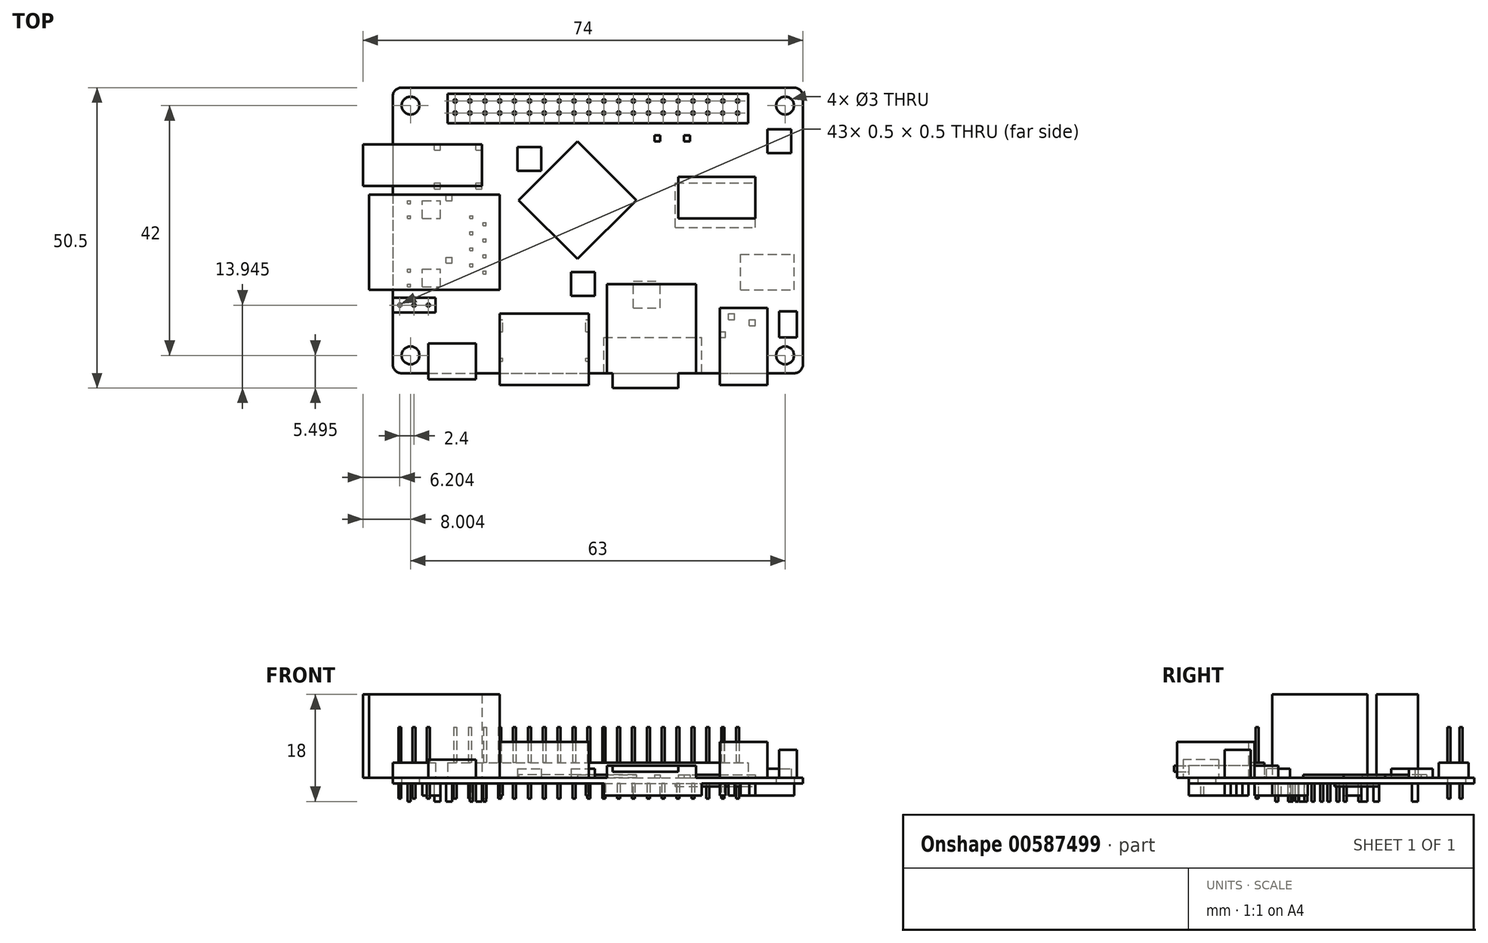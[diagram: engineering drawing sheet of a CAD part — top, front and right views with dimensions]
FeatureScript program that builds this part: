
annotation { "Feature Type Name" : "Feature", "Feature Type Description" : "" }
export const myFeature = defineFeature(function(context is Context, id is Id, definition is map)
    precondition{}
    {
        {
            var Q0;
            Q0=qCreatedBy(makeId("Top.planeOp"),FACE);
            var sketch = newSketch(context, id + "F0", { "sketchPlane" : qUnion([Q0])});
            skLineSegment(sketch, "E0.bottom", {"start": v(-42.34, 28.44) * mm, "end": v(23.66, 28.44) * mm});
            skLineSegment(sketch, "E0.top", {"start": v(-42.34, -19.56) * mm, "end": v(23.66, -19.56) * mm});
            skLineSegment(sketch, "E0.left", {"start": v(-43.84, 26.94) * mm, "end": v(-43.84, -18.06) * mm});
            skLineSegment(sketch, "E0.right", {"start": v(25.16, 26.94) * mm, "end": v(25.16, -18.06) * mm});
            skPoint(sketch, "E1", {"position": v(-43.84, 28.44) * mm});
            skCircle(sketch, "E2", {"center": v(-40.84, 25.44) * mm, "radius": 1.5 * mm});
            skCircle(sketch, "E3", {"center": v(22.16, 25.44) * mm, "radius": 1.5 * mm});
            skCircle(sketch, "E4", {"center": v(22.16, -16.56) * mm, "radius": 1.5 * mm});
            skCircle(sketch, "E5", {"center": v(-40.84, -16.56) * mm, "radius": 1.5 * mm});
            skLineSegment(sketch, "E6.bottom", {"start": v(-37.84, -19.56) * mm, "end": v(19.16, -19.56) * mm});
            skPoint(sketch, "E7.visualSharp", {"position": v(25.16, 28.44) * mm});
            skArc(sketch, "E7.filletArc", {"start": v(25.16, 26.94) * mm, "mid": v(24.72, 28) * mm, "end": v(23.66, 28.44) * mm});
            skArc(sketch, "E8.filletArc", {"start": v(-42.34, 28.44) * mm, "mid": v(-43.4, 28) * mm, "end": v(-43.84, 26.94) * mm});
            skPoint(sketch, "E9.visualSharp", {"position": v(-43.84, -19.56) * mm});
            skArc(sketch, "E9.filletArc", {"start": v(-43.84, -18.06) * mm, "mid": v(-43.4, -19.13) * mm, "end": v(-42.34, -19.56) * mm});
            skPoint(sketch, "E10.visualSharp", {"position": v(25.16, -19.56) * mm});
            skArc(sketch, "E10.filletArc", {"start": v(23.66, -19.56) * mm, "mid": v(24.72, -19.13) * mm, "end": v(25.16, -18.06) * mm});
            skSolve(sketch);
        }
        {
            var Q0;
            Q0=makeQuery(id+"F0.imprint","IMPRINT",FACE,{"disambiguationData":[TD([[makeQuery(id+"F0.imprint","IMPRINT",EDGE,{"derivedFrom":sQuery(id+"F0.wireOp",EDGE,"E0.bottom")}),-1.0]])]});
            extrude(context, id + "F1", {"entities" : qUnion([Q0]), "depth" : 1 * mm});
        }
        {
            var Q0;
            Q0=makeQuery(id+"F1.opExtrude","CAP_FACE",FACE,{"disambiguationData":[OSD([sQuery(id+"F0.wireOp",EDGE,"E0.bottom"),sQuery(id+"F0.wireOp",EDGE,"E0.top"),sQuery(id+"F0.wireOp",EDGE,"E0.left"),sQuery(id+"F0.wireOp",EDGE,"E0.right"),sQuery(id+"F0.wireOp",EDGE,"E2"),sQuery(id+"F0.wireOp",EDGE,"E3"),sQuery(id+"F0.wireOp",EDGE,"E4"),sQuery(id+"F0.wireOp",EDGE,"E5"),sQuery(id+"F0.wireOp",EDGE,"E6.bottom"),sQuery(id+"F0.wireOp",EDGE,"E7.filletArc"),sQuery(id+"F0.wireOp",EDGE,"E8.filletArc"),sQuery(id+"F0.wireOp",EDGE,"E9.filletArc"),sQuery(id+"F0.wireOp",EDGE,"E10.filletArc")])],"isStart":false});
            var sketch = newSketch(context, id + "F2", { "sketchPlane" : qUnion([Q0])});
            skLineSegment(sketch, "E11.bottom", {"start": v(24.16, -13.56) * mm, "end": v(21.16, -13.56) * mm});
            skLineSegment(sketch, "E11.top", {"start": v(24.16, -9.16) * mm, "end": v(21.16, -9.16) * mm});
            skLineSegment(sketch, "E11.left", {"start": v(24.16, -13.56) * mm, "end": v(24.16, -9.16) * mm});
            skLineSegment(sketch, "E11.right", {"start": v(21.16, -13.56) * mm, "end": v(21.16, -9.16) * mm});
            skSolve(sketch);
        }
        {
            var Q0;
            Q0=makeQuery(id+"F2.imprint","IMPRINT",FACE,{"disambiguationData":[TD([[makeQuery(id+"F2.imprint","IMPRINT",EDGE,{"derivedFrom":sQuery(id+"F2.wireOp",EDGE,"E11.bottom")}),-1.0]])]});
            extrude(context, id + "F3", {"entities" : qUnion([Q0]), "operationType" : NewBodyOperationType.ADD, "depth" : 4.7 * mm});
        }
        {
            var Q0;
            Q0=makeQuery(id+"F3.opExtrude","SWEPT_FACE",FACE,{"disambiguationData":[OSD([sQuery(id+"F2.wireOp",EDGE,"E11.left")])]});
            var sketch = newSketch(context, id + "F4", { "sketchPlane" : qUnion([Q0])});
            skCircle(sketch, "E12", {"center": v(-11.39, 3.44) * mm, "radius": 1.05 * mm});
            skSolve(sketch);
        }
        {
            var Q0;
            Q0=sQuery(id+"F4.wireOp",EDGE,"E12");
            extrude(context, id + "F5", {"bodyType" : ToolBodyType.SURFACE, "surfaceEntities" : qUnion([Q0]), "depth" : 2 * mm});
        }
        {
            var Q0;
            Q0=makeQuery(id+"F1.opExtrude","CAP_FACE",FACE,{"disambiguationData":[OSD([sQuery(id+"F0.wireOp",EDGE,"E0.bottom"),sQuery(id+"F0.wireOp",EDGE,"E0.top"),sQuery(id+"F0.wireOp",EDGE,"E0.left"),sQuery(id+"F0.wireOp",EDGE,"E0.right"),sQuery(id+"F0.wireOp",EDGE,"E2"),sQuery(id+"F0.wireOp",EDGE,"E3"),sQuery(id+"F0.wireOp",EDGE,"E4"),sQuery(id+"F0.wireOp",EDGE,"E5"),sQuery(id+"F0.wireOp",EDGE,"E6.bottom"),sQuery(id+"F0.wireOp",EDGE,"E7.filletArc"),sQuery(id+"F0.wireOp",EDGE,"E8.filletArc"),sQuery(id+"F0.wireOp",EDGE,"E9.filletArc"),sQuery(id+"F0.wireOp",EDGE,"E10.filletArc")])],"isStart":false});
            var sketch = newSketch(context, id + "F6", { "sketchPlane" : qUnion([Q0])});
            skLineSegment(sketch, "E13.bottom", {"start": v(11.16, -8.56) * mm, "end": v(19.16, -8.56) * mm});
            skLineSegment(sketch, "E13.top", {"start": v(11.16, -21.56) * mm, "end": v(19.16, -21.56) * mm});
            skLineSegment(sketch, "E13.left", {"start": v(11.16, -8.56) * mm, "end": v(11.16, -21.56) * mm});
            skLineSegment(sketch, "E13.right", {"start": v(19.16, -8.56) * mm, "end": v(19.16, -21.56) * mm});
            skSolve(sketch);
        }
        {
            var Q0;
            Q0=qSketchRegion(id+"F6",true);
            extrude(context, id + "F7", {"entities" : qUnion([Q0]), "operationType" : NewBodyOperationType.ADD, "depth" : 6 * mm});
        }
        {
            var Q0;
            Q0=makeQuery(id+"F1.opExtrude","CAP_FACE",FACE,{"disambiguationData":[OSD([sQuery(id+"F0.wireOp",EDGE,"E0.bottom"),sQuery(id+"F0.wireOp",EDGE,"E0.top"),sQuery(id+"F0.wireOp",EDGE,"E0.left"),sQuery(id+"F0.wireOp",EDGE,"E0.right"),sQuery(id+"F0.wireOp",EDGE,"E2"),sQuery(id+"F0.wireOp",EDGE,"E3"),sQuery(id+"F0.wireOp",EDGE,"E4"),sQuery(id+"F0.wireOp",EDGE,"E5"),sQuery(id+"F0.wireOp",EDGE,"E6.bottom"),sQuery(id+"F0.wireOp",EDGE,"E7.filletArc"),sQuery(id+"F0.wireOp",EDGE,"E8.filletArc"),sQuery(id+"F0.wireOp",EDGE,"E9.filletArc"),sQuery(id+"F0.wireOp",EDGE,"E10.filletArc")])],"isStart":false});
            var sketch = newSketch(context, id + "F8", { "sketchPlane" : qUnion([Q0])});
            skLineSegment(sketch, "E14.bottom", {"start": v(-7.84, -4.56) * mm, "end": v(7.16, -4.56) * mm});
            skLineSegment(sketch, "E14.top", {"start": v(-7.84, -19.56) * mm, "end": v(7.16, -19.56) * mm});
            skLineSegment(sketch, "E14.left", {"start": v(-7.84, -4.56) * mm, "end": v(-7.84, -19.56) * mm});
            skLineSegment(sketch, "E14.right", {"start": v(7.16, -4.56) * mm, "end": v(7.16, -19.56) * mm});
            skSolve(sketch);
        }
        {
            var Q0;
            Q0=qSketchRegion(id+"F8",true);
            extrude(context, id + "F9", {"entities" : qUnion([Q0]), "operationType" : NewBodyOperationType.ADD, "depth" : 2 * mm});
        }
        {
            var Q0;
            Q0=makeQuery(id+"F9.boolean.opBoolean","MERGE",FACE,{"derivedFrom":[makeQuery(id+"F1.opExtrude","SWEPT_FACE",FACE,{"disambiguationData":[OSD([sQuery(id+"F0.wireOp",EDGE,"E0.top"),sQuery(id+"F0.wireOp",EDGE,"E6.bottom")])]}),makeQuery(id+"F9.opExtrude","SWEPT_FACE",FACE,{"disambiguationData":[OSD([sQuery(id+"F8.wireOp",EDGE,"E14.top")])]})]});
            var sketch = newSketch(context, id + "F10", { "sketchPlane" : qUnion([Q0])});
            skLineSegment(sketch, "E15.bottom", {"start": v(-6.84, 3) * mm, "end": v(4.16, 3) * mm});
            skLineSegment(sketch, "E15.top", {"start": v(-6.84, 2) * mm, "end": v(4.16, 2) * mm});
            skLineSegment(sketch, "E15.left", {"start": v(-6.84, 3) * mm, "end": v(-6.84, 2) * mm});
            skLineSegment(sketch, "E15.right", {"start": v(4.16, 3) * mm, "end": v(4.16, 2) * mm});
            skSolve(sketch);
        }
        {
            var Q0;
            Q0=qSketchRegion(id+"F10",true);
            extrude(context, id + "F11", {"entities" : qUnion([Q0]), "operationType" : NewBodyOperationType.ADD, "depth" : 2.5 * mm});
        }
        {
            var Q0;
            Q0=makeQuery(id+"F1.opExtrude","CAP_FACE",FACE,{"disambiguationData":[OSD([sQuery(id+"F0.wireOp",EDGE,"E0.bottom"),sQuery(id+"F0.wireOp",EDGE,"E0.top"),sQuery(id+"F0.wireOp",EDGE,"E0.left"),sQuery(id+"F0.wireOp",EDGE,"E0.right"),sQuery(id+"F0.wireOp",EDGE,"E2"),sQuery(id+"F0.wireOp",EDGE,"E3"),sQuery(id+"F0.wireOp",EDGE,"E4"),sQuery(id+"F0.wireOp",EDGE,"E5"),sQuery(id+"F0.wireOp",EDGE,"E6.bottom"),sQuery(id+"F0.wireOp",EDGE,"E7.filletArc"),sQuery(id+"F0.wireOp",EDGE,"E8.filletArc"),sQuery(id+"F0.wireOp",EDGE,"E9.filletArc"),sQuery(id+"F0.wireOp",EDGE,"E10.filletArc")])],"isStart":false});
            var sketch = newSketch(context, id + "F12", { "sketchPlane" : qUnion([Q0])});
            skLineSegment(sketch, "E16.bottom", {"start": v(-25.84, -9.56) * mm, "end": v(-10.84, -9.56) * mm});
            skLineSegment(sketch, "E16.top", {"start": v(-25.84, -21.56) * mm, "end": v(-10.84, -21.56) * mm});
            skLineSegment(sketch, "E16.left", {"start": v(-25.84, -9.56) * mm, "end": v(-25.84, -21.56) * mm});
            skLineSegment(sketch, "E16.right", {"start": v(-10.84, -9.56) * mm, "end": v(-10.84, -21.56) * mm});
            skSolve(sketch);
        }
        {
            var Q0;
            Q0=qSketchRegion(id+"F12",true);
            extrude(context, id + "F13", {"entities" : qUnion([Q0]), "operationType" : NewBodyOperationType.ADD, "depth" : 6 * mm});
        }
        {
            var Q0;
            Q0=makeQuery(id+"F1.opExtrude","CAP_FACE",FACE,{"disambiguationData":[OSD([sQuery(id+"F0.wireOp",EDGE,"E0.bottom"),sQuery(id+"F0.wireOp",EDGE,"E0.top"),sQuery(id+"F0.wireOp",EDGE,"E0.left"),sQuery(id+"F0.wireOp",EDGE,"E0.right"),sQuery(id+"F0.wireOp",EDGE,"E2"),sQuery(id+"F0.wireOp",EDGE,"E3"),sQuery(id+"F0.wireOp",EDGE,"E4"),sQuery(id+"F0.wireOp",EDGE,"E5"),sQuery(id+"F0.wireOp",EDGE,"E6.bottom"),sQuery(id+"F0.wireOp",EDGE,"E7.filletArc"),sQuery(id+"F0.wireOp",EDGE,"E8.filletArc"),sQuery(id+"F0.wireOp",EDGE,"E9.filletArc"),sQuery(id+"F0.wireOp",EDGE,"E10.filletArc")])],"isStart":false});
            var sketch = newSketch(context, id + "F14", { "sketchPlane" : qUnion([Q0])});
            skLineSegment(sketch, "E17.bottom", {"start": v(-37.84, -14.56) * mm, "end": v(-29.84, -14.56) * mm});
            skLineSegment(sketch, "E17.top", {"start": v(-37.84, -20.56) * mm, "end": v(-29.84, -20.56) * mm});
            skLineSegment(sketch, "E17.left", {"start": v(-37.84, -14.56) * mm, "end": v(-37.84, -20.56) * mm});
            skLineSegment(sketch, "E17.right", {"start": v(-29.84, -14.56) * mm, "end": v(-29.84, -20.56) * mm});
            skSolve(sketch);
        }
        {
            var Q0;
            Q0=qSketchRegion(id+"F14",true);
            extrude(context, id + "F15", {"entities" : qUnion([Q0]), "operationType" : NewBodyOperationType.ADD, "depth" : 3 * mm});
        }
        {
            var Q0;
            Q0=makeQuery(id+"F1.opExtrude","CAP_FACE",FACE,{"disambiguationData":[OSD([sQuery(id+"F0.wireOp",EDGE,"E0.bottom"),sQuery(id+"F0.wireOp",EDGE,"E0.top"),sQuery(id+"F0.wireOp",EDGE,"E0.left"),sQuery(id+"F0.wireOp",EDGE,"E0.right"),sQuery(id+"F0.wireOp",EDGE,"E2"),sQuery(id+"F0.wireOp",EDGE,"E3"),sQuery(id+"F0.wireOp",EDGE,"E4"),sQuery(id+"F0.wireOp",EDGE,"E5"),sQuery(id+"F0.wireOp",EDGE,"E6.bottom"),sQuery(id+"F0.wireOp",EDGE,"E7.filletArc"),sQuery(id+"F0.wireOp",EDGE,"E8.filletArc"),sQuery(id+"F0.wireOp",EDGE,"E9.filletArc"),sQuery(id+"F0.wireOp",EDGE,"E10.filletArc")])],"isStart":false});
            var sketch = newSketch(context, id + "F16", { "sketchPlane" : qUnion([Q0])});
            skLineSegment(sketch, "E18.bottom", {"start": v(-43.84, -6.86) * mm, "end": v(-36.64, -6.86) * mm});
            skLineSegment(sketch, "E18.top", {"start": v(-43.84, -9.36) * mm, "end": v(-36.64, -9.36) * mm});
            skLineSegment(sketch, "E18.left", {"start": v(-43.84, -6.86) * mm, "end": v(-43.84, -9.36) * mm});
            skLineSegment(sketch, "E18.right", {"start": v(-36.64, -6.86) * mm, "end": v(-36.64, -9.36) * mm});
            skSolve(sketch);
        }
        {
            var Q0;
            Q0=qSketchRegion(id+"F16",true);
            extrude(context, id + "F17", {"entities" : qUnion([Q0]), "operationType" : NewBodyOperationType.ADD, "depth" : 2.5 * mm});
        }
        {
            var Q0;
            Q0=makeQuery(id+"F17.opExtrude","CAP_FACE",FACE,{"disambiguationData":[OSD([sQuery(id+"F16.wireOp",EDGE,"E18.bottom"),sQuery(id+"F16.wireOp",EDGE,"E18.top"),sQuery(id+"F16.wireOp",EDGE,"E18.left"),sQuery(id+"F16.wireOp",EDGE,"E18.right")])],"isStart":false});
            var sketch = newSketch(context, id + "F18", { "sketchPlane" : qUnion([Q0])});
            skLineSegment(sketch, "E19.bottom", {"start": v(-42.89, -7.86) * mm, "end": v(-42.39, -7.86) * mm});
            skLineSegment(sketch, "E19.top", {"start": v(-42.89, -8.36) * mm, "end": v(-42.39, -8.36) * mm});
            skLineSegment(sketch, "E19.left", {"start": v(-42.89, -7.86) * mm, "end": v(-42.89, -8.36) * mm});
            skLineSegment(sketch, "E19.right", {"start": v(-42.39, -7.86) * mm, "end": v(-42.39, -8.36) * mm});
            skLineSegment(sketch, "E20.bottom", {"start": v(-40.49, -7.86) * mm, "end": v(-39.99, -7.86) * mm});
            skLineSegment(sketch, "E20.top", {"start": v(-40.49, -8.36) * mm, "end": v(-39.99, -8.36) * mm});
            skLineSegment(sketch, "E20.left", {"start": v(-40.49, -7.86) * mm, "end": v(-40.49, -8.36) * mm});
            skLineSegment(sketch, "E20.right", {"start": v(-39.99, -7.86) * mm, "end": v(-39.99, -8.36) * mm});
            skLineSegment(sketch, "E21.bottom", {"start": v(-38.09, -7.86) * mm, "end": v(-37.59, -7.86) * mm});
            skLineSegment(sketch, "E21.top", {"start": v(-38.09, -8.36) * mm, "end": v(-37.59, -8.36) * mm});
            skLineSegment(sketch, "E21.left", {"start": v(-38.09, -7.86) * mm, "end": v(-38.09, -8.36) * mm});
            skLineSegment(sketch, "E21.right", {"start": v(-37.59, -7.86) * mm, "end": v(-37.59, -8.36) * mm});
            skSolve(sketch);
        }
        {
            var Q0;
            Q0=qSketchRegion(id+"F18",true);
            extrude(context, id + "F19", {"entities" : qUnion([Q0]), "operationType" : NewBodyOperationType.ADD, "depth" : 6 * mm});
        }
        {
            var Q0;
            Q0=makeQuery(id+"F1.opExtrude","CAP_FACE",FACE,{"disambiguationData":[OSD([sQuery(id+"F0.wireOp",EDGE,"E0.bottom"),sQuery(id+"F0.wireOp",EDGE,"E0.top"),sQuery(id+"F0.wireOp",EDGE,"E0.left"),sQuery(id+"F0.wireOp",EDGE,"E0.right"),sQuery(id+"F0.wireOp",EDGE,"E2"),sQuery(id+"F0.wireOp",EDGE,"E3"),sQuery(id+"F0.wireOp",EDGE,"E4"),sQuery(id+"F0.wireOp",EDGE,"E5"),sQuery(id+"F0.wireOp",EDGE,"E6.bottom"),sQuery(id+"F0.wireOp",EDGE,"E7.filletArc"),sQuery(id+"F0.wireOp",EDGE,"E8.filletArc"),sQuery(id+"F0.wireOp",EDGE,"E9.filletArc"),sQuery(id+"F0.wireOp",EDGE,"E10.filletArc")])],"isStart":false});
            var sketch = newSketch(context, id + "F20", { "sketchPlane" : qUnion([Q0])});
            skLineSegment(sketch, "E22.bottom", {"start": v(-25.84, 10.44) * mm, "end": v(-47.84, 10.44) * mm});
            skLineSegment(sketch, "E22.top", {"start": v(-25.84, -5.56) * mm, "end": v(-47.84, -5.56) * mm});
            skLineSegment(sketch, "E22.left", {"start": v(-25.84, 10.44) * mm, "end": v(-25.84, -5.56) * mm});
            skLineSegment(sketch, "E22.right", {"start": v(-47.84, 10.44) * mm, "end": v(-47.84, -5.56) * mm});
            skSolve(sketch);
        }
        {
            var Q0;
            Q0=qSketchRegion(id+"F20",true);
            extrude(context, id + "F21", {"entities" : qUnion([Q0]), "operationType" : NewBodyOperationType.ADD, "depth" : 14 * mm});
        }
        {
            var Q0;
            Q0=makeQuery(id+"F1.opExtrude","CAP_FACE",FACE,{"disambiguationData":[OSD([sQuery(id+"F0.wireOp",EDGE,"E0.bottom"),sQuery(id+"F0.wireOp",EDGE,"E0.top"),sQuery(id+"F0.wireOp",EDGE,"E0.left"),sQuery(id+"F0.wireOp",EDGE,"E0.right"),sQuery(id+"F0.wireOp",EDGE,"E2"),sQuery(id+"F0.wireOp",EDGE,"E3"),sQuery(id+"F0.wireOp",EDGE,"E4"),sQuery(id+"F0.wireOp",EDGE,"E5"),sQuery(id+"F0.wireOp",EDGE,"E6.bottom"),sQuery(id+"F0.wireOp",EDGE,"E7.filletArc"),sQuery(id+"F0.wireOp",EDGE,"E8.filletArc"),sQuery(id+"F0.wireOp",EDGE,"E9.filletArc"),sQuery(id+"F0.wireOp",EDGE,"E10.filletArc")])],"isStart":false});
            var sketch = newSketch(context, id + "F22", { "sketchPlane" : qUnion([Q0])});
            skLineSegment(sketch, "E23.bottom", {"start": v(-48.84, 18.94) * mm, "end": v(-28.84, 18.94) * mm});
            skLineSegment(sketch, "E23.top", {"start": v(-48.84, 11.94) * mm, "end": v(-28.84, 11.94) * mm});
            skLineSegment(sketch, "E23.left", {"start": v(-48.84, 18.94) * mm, "end": v(-48.84, 11.94) * mm});
            skLineSegment(sketch, "E23.right", {"start": v(-28.84, 18.94) * mm, "end": v(-28.84, 11.94) * mm});
            skSolve(sketch);
        }
        {
            var Q0;
            Q0=qSketchRegion(id+"F22",true);
            extrude(context, id + "F23", {"entities" : qUnion([Q0]), "operationType" : NewBodyOperationType.ADD, "depth" : 14 * mm});
        }
        {
            var Q0;
            Q0=makeQuery(id+"F1.opExtrude","CAP_FACE",FACE,{"disambiguationData":[OSD([sQuery(id+"F0.wireOp",EDGE,"E0.bottom"),sQuery(id+"F0.wireOp",EDGE,"E0.top"),sQuery(id+"F0.wireOp",EDGE,"E0.left"),sQuery(id+"F0.wireOp",EDGE,"E0.right"),sQuery(id+"F0.wireOp",EDGE,"E2"),sQuery(id+"F0.wireOp",EDGE,"E3"),sQuery(id+"F0.wireOp",EDGE,"E4"),sQuery(id+"F0.wireOp",EDGE,"E5"),sQuery(id+"F0.wireOp",EDGE,"E6.bottom"),sQuery(id+"F0.wireOp",EDGE,"E7.filletArc"),sQuery(id+"F0.wireOp",EDGE,"E8.filletArc"),sQuery(id+"F0.wireOp",EDGE,"E9.filletArc"),sQuery(id+"F0.wireOp",EDGE,"E10.filletArc")])],"isStart":false});
            var sketch = newSketch(context, id + "F24", { "sketchPlane" : qUnion([Q0])});
            skLineSegment(sketch, "E24.bottom", {"start": v(-34.59, 27.44) * mm, "end": v(15.91, 27.44) * mm});
            skLineSegment(sketch, "E24.top", {"start": v(-34.59, 22.44) * mm, "end": v(15.91, 22.44) * mm});
            skLineSegment(sketch, "E24.left", {"start": v(-34.59, 27.44) * mm, "end": v(-34.59, 22.44) * mm});
            skLineSegment(sketch, "E24.right", {"start": v(15.91, 27.44) * mm, "end": v(15.91, 22.44) * mm});
            skSolve(sketch);
        }
        {
            var Q0;
            Q0=qSketchRegion(id+"F24",true);
            extrude(context, id + "F25", {"entities" : qUnion([Q0]), "operationType" : NewBodyOperationType.ADD, "depth" : 2.5 * mm});
        }
        {
            var Q0;
            Q0=makeQuery(id+"F25.opExtrude","CAP_FACE",FACE,{"disambiguationData":[OSD([sQuery(id+"F24.wireOp",EDGE,"E24.bottom"),sQuery(id+"F24.wireOp",EDGE,"E24.top"),sQuery(id+"F24.wireOp",EDGE,"E24.left"),sQuery(id+"F24.wireOp",EDGE,"E24.right")])],"isStart":false});
            var sketch = newSketch(context, id + "F26", { "sketchPlane" : qUnion([Q0])});
            skLineSegment(sketch, "E25.bottom", {"start": v(-33.59, 26.44) * mm, "end": v(-33.09, 26.44) * mm});
            skLineSegment(sketch, "E25.top", {"start": v(-33.59, 25.94) * mm, "end": v(-33.09, 25.94) * mm});
            skLineSegment(sketch, "E25.left", {"start": v(-33.59, 26.44) * mm, "end": v(-33.59, 25.94) * mm});
            skLineSegment(sketch, "E25.right", {"start": v(-33.09, 26.44) * mm, "end": v(-33.09, 25.94) * mm});
            skLineSegment(sketch, "E26.1.0.0", {"start": v(-31.09, 26.44) * mm, "end": v(-31.09, 25.94) * mm});
            skLineSegment(sketch, "E26.1.0.1", {"start": v(-31.09, 26.44) * mm, "end": v(-30.59, 26.44) * mm});
            skLineSegment(sketch, "E26.1.0.2", {"start": v(-30.59, 26.44) * mm, "end": v(-30.59, 25.94) * mm});
            skLineSegment(sketch, "E26.1.0.3", {"start": v(-31.09, 25.94) * mm, "end": v(-30.59, 25.94) * mm});
            skLineSegment(sketch, "E26.2.0.0", {"start": v(-28.59, 26.44) * mm, "end": v(-28.59, 25.94) * mm});
            skLineSegment(sketch, "E26.2.0.1", {"start": v(-28.59, 26.44) * mm, "end": v(-28.09, 26.44) * mm});
            skLineSegment(sketch, "E26.2.0.2", {"start": v(-28.09, 26.44) * mm, "end": v(-28.09, 25.94) * mm});
            skLineSegment(sketch, "E26.2.0.3", {"start": v(-28.59, 25.94) * mm, "end": v(-28.09, 25.94) * mm});
            skLineSegment(sketch, "E26.direction1", {"start": v(-33.59, 25.94) * mm, "end": v(-31.09, 25.94) * mm, "construction": true});
            skLineSegment(sketch, "E27.0.3.0", {"start": v(-26.09, 26.44) * mm, "end": v(-26.09, 25.94) * mm});
            skLineSegment(sketch, "E27.3.3.0", {"start": v(-26.09, 26.44) * mm, "end": v(-25.59, 26.44) * mm});
            skLineSegment(sketch, "E27.6.3.0", {"start": v(-25.59, 26.44) * mm, "end": v(-25.59, 25.94) * mm});
            skLineSegment(sketch, "E27.9.3.0", {"start": v(-26.09, 25.94) * mm, "end": v(-25.59, 25.94) * mm});
            skLineSegment(sketch, "E27.0.4.0", {"start": v(-23.59, 26.44) * mm, "end": v(-23.59, 25.94) * mm});
            skLineSegment(sketch, "E27.3.4.0", {"start": v(-23.59, 26.44) * mm, "end": v(-23.09, 26.44) * mm});
            skLineSegment(sketch, "E27.6.4.0", {"start": v(-23.09, 26.44) * mm, "end": v(-23.09, 25.94) * mm});
            skLineSegment(sketch, "E27.9.4.0", {"start": v(-23.59, 25.94) * mm, "end": v(-23.09, 25.94) * mm});
            skLineSegment(sketch, "E27.0.5.0", {"start": v(-21.09, 26.44) * mm, "end": v(-21.09, 25.94) * mm});
            skLineSegment(sketch, "E27.3.5.0", {"start": v(-21.09, 26.44) * mm, "end": v(-20.59, 26.44) * mm});
            skLineSegment(sketch, "E27.6.5.0", {"start": v(-20.59, 26.44) * mm, "end": v(-20.59, 25.94) * mm});
            skLineSegment(sketch, "E27.9.5.0", {"start": v(-21.09, 25.94) * mm, "end": v(-20.59, 25.94) * mm});
            skLineSegment(sketch, "E27.0.6.0", {"start": v(-18.59, 26.44) * mm, "end": v(-18.59, 25.94) * mm});
            skLineSegment(sketch, "E27.3.6.0", {"start": v(-18.59, 26.44) * mm, "end": v(-18.09, 26.44) * mm});
            skLineSegment(sketch, "E27.6.6.0", {"start": v(-18.09, 26.44) * mm, "end": v(-18.09, 25.94) * mm});
            skLineSegment(sketch, "E27.9.6.0", {"start": v(-18.59, 25.94) * mm, "end": v(-18.09, 25.94) * mm});
            skLineSegment(sketch, "E27.0.7.0", {"start": v(-16.09, 26.44) * mm, "end": v(-16.09, 25.94) * mm});
            skLineSegment(sketch, "E27.3.7.0", {"start": v(-16.09, 26.44) * mm, "end": v(-15.59, 26.44) * mm});
            skLineSegment(sketch, "E27.6.7.0", {"start": v(-15.59, 26.44) * mm, "end": v(-15.59, 25.94) * mm});
            skLineSegment(sketch, "E27.9.7.0", {"start": v(-16.09, 25.94) * mm, "end": v(-15.59, 25.94) * mm});
            skLineSegment(sketch, "E27.0.8.0", {"start": v(-13.59, 26.44) * mm, "end": v(-13.59, 25.94) * mm});
            skLineSegment(sketch, "E27.3.8.0", {"start": v(-13.59, 26.44) * mm, "end": v(-13.09, 26.44) * mm});
            skLineSegment(sketch, "E27.6.8.0", {"start": v(-13.09, 26.44) * mm, "end": v(-13.09, 25.94) * mm});
            skLineSegment(sketch, "E27.9.8.0", {"start": v(-13.59, 25.94) * mm, "end": v(-13.09, 25.94) * mm});
            skLineSegment(sketch, "E27.0.9.0", {"start": v(-11.09, 26.44) * mm, "end": v(-11.09, 25.94) * mm});
            skLineSegment(sketch, "E27.3.9.0", {"start": v(-11.09, 26.44) * mm, "end": v(-10.59, 26.44) * mm});
            skLineSegment(sketch, "E27.6.9.0", {"start": v(-10.59, 26.44) * mm, "end": v(-10.59, 25.94) * mm});
            skLineSegment(sketch, "E27.9.9.0", {"start": v(-11.09, 25.94) * mm, "end": v(-10.59, 25.94) * mm});
            skLineSegment(sketch, "E27.0.10.0", {"start": v(-8.59, 26.44) * mm, "end": v(-8.59, 25.94) * mm});
            skLineSegment(sketch, "E27.3.10.0", {"start": v(-8.59, 26.44) * mm, "end": v(-8.09, 26.44) * mm});
            skLineSegment(sketch, "E27.6.10.0", {"start": v(-8.09, 26.44) * mm, "end": v(-8.09, 25.94) * mm});
            skLineSegment(sketch, "E27.9.10.0", {"start": v(-8.59, 25.94) * mm, "end": v(-8.09, 25.94) * mm});
            skLineSegment(sketch, "E27.0.11.0", {"start": v(-6.09, 26.44) * mm, "end": v(-6.09, 25.94) * mm});
            skLineSegment(sketch, "E27.3.11.0", {"start": v(-6.09, 26.44) * mm, "end": v(-5.59, 26.44) * mm});
            skLineSegment(sketch, "E27.6.11.0", {"start": v(-5.59, 26.44) * mm, "end": v(-5.59, 25.94) * mm});
            skLineSegment(sketch, "E27.9.11.0", {"start": v(-6.09, 25.94) * mm, "end": v(-5.59, 25.94) * mm});
            skLineSegment(sketch, "E27.0.12.0", {"start": v(-3.59, 26.44) * mm, "end": v(-3.59, 25.94) * mm});
            skLineSegment(sketch, "E27.3.12.0", {"start": v(-3.59, 26.44) * mm, "end": v(-3.09, 26.44) * mm});
            skLineSegment(sketch, "E27.6.12.0", {"start": v(-3.09, 26.44) * mm, "end": v(-3.09, 25.94) * mm});
            skLineSegment(sketch, "E27.9.12.0", {"start": v(-3.59, 25.94) * mm, "end": v(-3.09, 25.94) * mm});
            skLineSegment(sketch, "E27.0.13.0", {"start": v(-1.09, 26.44) * mm, "end": v(-1.09, 25.94) * mm});
            skLineSegment(sketch, "E27.3.13.0", {"start": v(-1.09, 26.44) * mm, "end": v(-0.59, 26.44) * mm});
            skLineSegment(sketch, "E27.6.13.0", {"start": v(-0.59, 26.44) * mm, "end": v(-0.59, 25.94) * mm});
            skLineSegment(sketch, "E27.9.13.0", {"start": v(-1.09, 25.94) * mm, "end": v(-0.59, 25.94) * mm});
            skLineSegment(sketch, "E27.0.14.0", {"start": v(1.41, 26.44) * mm, "end": v(1.41, 25.94) * mm});
            skLineSegment(sketch, "E27.3.14.0", {"start": v(1.41, 26.44) * mm, "end": v(1.91, 26.44) * mm});
            skLineSegment(sketch, "E27.6.14.0", {"start": v(1.91, 26.44) * mm, "end": v(1.91, 25.94) * mm});
            skLineSegment(sketch, "E27.9.14.0", {"start": v(1.41, 25.94) * mm, "end": v(1.91, 25.94) * mm});
            skLineSegment(sketch, "E27.0.15.0", {"start": v(3.91, 26.44) * mm, "end": v(3.91, 25.94) * mm});
            skLineSegment(sketch, "E27.3.15.0", {"start": v(3.91, 26.44) * mm, "end": v(4.41, 26.44) * mm});
            skLineSegment(sketch, "E27.6.15.0", {"start": v(4.41, 26.44) * mm, "end": v(4.41, 25.94) * mm});
            skLineSegment(sketch, "E27.9.15.0", {"start": v(3.91, 25.94) * mm, "end": v(4.41, 25.94) * mm});
            skLineSegment(sketch, "E27.0.16.0", {"start": v(6.41, 26.44) * mm, "end": v(6.41, 25.94) * mm});
            skLineSegment(sketch, "E27.3.16.0", {"start": v(6.41, 26.44) * mm, "end": v(6.91, 26.44) * mm});
            skLineSegment(sketch, "E27.6.16.0", {"start": v(6.91, 26.44) * mm, "end": v(6.91, 25.94) * mm});
            skLineSegment(sketch, "E27.9.16.0", {"start": v(6.41, 25.94) * mm, "end": v(6.91, 25.94) * mm});
            skLineSegment(sketch, "E27.0.17.0", {"start": v(8.91, 26.44) * mm, "end": v(8.91, 25.94) * mm});
            skLineSegment(sketch, "E27.3.17.0", {"start": v(8.91, 26.44) * mm, "end": v(9.41, 26.44) * mm});
            skLineSegment(sketch, "E27.6.17.0", {"start": v(9.41, 26.44) * mm, "end": v(9.41, 25.94) * mm});
            skLineSegment(sketch, "E27.9.17.0", {"start": v(8.91, 25.94) * mm, "end": v(9.41, 25.94) * mm});
            skLineSegment(sketch, "E27.0.18.0", {"start": v(11.41, 26.44) * mm, "end": v(11.41, 25.94) * mm});
            skLineSegment(sketch, "E27.3.18.0", {"start": v(11.41, 26.44) * mm, "end": v(11.91, 26.44) * mm});
            skLineSegment(sketch, "E27.6.18.0", {"start": v(11.91, 26.44) * mm, "end": v(11.91, 25.94) * mm});
            skLineSegment(sketch, "E27.9.18.0", {"start": v(11.41, 25.94) * mm, "end": v(11.91, 25.94) * mm});
            skLineSegment(sketch, "E27.0.19.0", {"start": v(13.91, 26.44) * mm, "end": v(13.91, 25.94) * mm});
            skLineSegment(sketch, "E27.3.19.0", {"start": v(13.91, 26.44) * mm, "end": v(14.41, 26.44) * mm});
            skLineSegment(sketch, "E27.6.19.0", {"start": v(14.41, 26.44) * mm, "end": v(14.41, 25.94) * mm});
            skLineSegment(sketch, "E27.9.19.0", {"start": v(13.91, 25.94) * mm, "end": v(14.41, 25.94) * mm});
            skLineSegment(sketch, "E28.direction1", {"start": v(13.91, 25.94) * mm, "end": v(13.9, 23.94) * mm, "construction": true});
            skLineSegment(sketch, "E29.0.1.0", {"start": v(13.9, 23.94) * mm, "end": v(14.4, 23.94) * mm});
            skLineSegment(sketch, "E29.3.1.0", {"start": v(14.4, 24.44) * mm, "end": v(14.4, 23.94) * mm});
            skLineSegment(sketch, "E29.6.1.0", {"start": v(13.9, 24.44) * mm, "end": v(14.4, 24.44) * mm});
            skLineSegment(sketch, "E29.9.1.0", {"start": v(13.9, 24.44) * mm, "end": v(13.9, 23.94) * mm});
            skLineSegment(sketch, "E30.1.0.0", {"start": v(11.4, 23.93) * mm, "end": v(11.9, 23.93) * mm});
            skLineSegment(sketch, "E30.1.0.1", {"start": v(11.41, 25.93) * mm, "end": v(11.4, 23.93) * mm, "construction": true});
            skLineSegment(sketch, "E30.1.0.2", {"start": v(11.9, 24.43) * mm, "end": v(11.9, 23.93) * mm});
            skLineSegment(sketch, "E30.1.0.3", {"start": v(11.4, 24.43) * mm, "end": v(11.9, 24.43) * mm});
            skLineSegment(sketch, "E30.2.0.0", {"start": v(8.9, 23.93) * mm, "end": v(9.4, 23.93) * mm});
            skLineSegment(sketch, "E30.2.0.1", {"start": v(8.91, 25.93) * mm, "end": v(8.9, 23.93) * mm, "construction": true});
            skLineSegment(sketch, "E30.2.0.2", {"start": v(9.4, 24.43) * mm, "end": v(9.4, 23.93) * mm});
            skLineSegment(sketch, "E30.2.0.3", {"start": v(8.9, 24.43) * mm, "end": v(9.4, 24.43) * mm});
            skLineSegment(sketch, "E30.direction1", {"start": v(13.9, 23.94) * mm, "end": v(11.4, 23.93) * mm, "construction": true});
            skLineSegment(sketch, "E31.0.3.0", {"start": v(6.4, 23.93) * mm, "end": v(6.9, 23.93) * mm});
            skLineSegment(sketch, "E31.3.3.0", {"start": v(6.41, 25.93) * mm, "end": v(6.4, 23.93) * mm, "construction": true});
            skLineSegment(sketch, "E31.6.3.0", {"start": v(6.9, 24.43) * mm, "end": v(6.9, 23.93) * mm});
            skLineSegment(sketch, "E31.9.3.0", {"start": v(6.4, 24.43) * mm, "end": v(6.9, 24.43) * mm});
            skLineSegment(sketch, "E31.0.4.0", {"start": v(3.9, 23.93) * mm, "end": v(4.4, 23.93) * mm});
            skLineSegment(sketch, "E31.3.4.0", {"start": v(3.91, 25.93) * mm, "end": v(3.9, 23.93) * mm, "construction": true});
            skLineSegment(sketch, "E31.6.4.0", {"start": v(4.4, 24.43) * mm, "end": v(4.4, 23.93) * mm});
            skLineSegment(sketch, "E31.9.4.0", {"start": v(3.9, 24.43) * mm, "end": v(4.4, 24.43) * mm});
            skLineSegment(sketch, "E31.0.5.0", {"start": v(1.4, 23.93) * mm, "end": v(1.9, 23.93) * mm});
            skLineSegment(sketch, "E31.3.5.0", {"start": v(1.41, 25.93) * mm, "end": v(1.4, 23.93) * mm, "construction": true});
            skLineSegment(sketch, "E31.6.5.0", {"start": v(1.9, 24.43) * mm, "end": v(1.9, 23.93) * mm});
            skLineSegment(sketch, "E31.9.5.0", {"start": v(1.4, 24.43) * mm, "end": v(1.9, 24.43) * mm});
            skLineSegment(sketch, "E31.0.6.0", {"start": v(-1.1, 23.93) * mm, "end": v(-0.6, 23.93) * mm});
            skLineSegment(sketch, "E31.3.6.0", {"start": v(-1.09, 25.93) * mm, "end": v(-1.1, 23.93) * mm, "construction": true});
            skLineSegment(sketch, "E31.6.6.0", {"start": v(-0.6, 24.43) * mm, "end": v(-0.6, 23.93) * mm});
            skLineSegment(sketch, "E31.9.6.0", {"start": v(-1.1, 24.43) * mm, "end": v(-0.6, 24.43) * mm});
            skLineSegment(sketch, "E31.0.7.0", {"start": v(-3.6, 23.93) * mm, "end": v(-3.1, 23.93) * mm});
            skLineSegment(sketch, "E31.3.7.0", {"start": v(-3.59, 25.93) * mm, "end": v(-3.6, 23.93) * mm, "construction": true});
            skLineSegment(sketch, "E31.6.7.0", {"start": v(-3.1, 24.43) * mm, "end": v(-3.1, 23.93) * mm});
            skLineSegment(sketch, "E31.9.7.0", {"start": v(-3.6, 24.43) * mm, "end": v(-3.1, 24.43) * mm});
            skLineSegment(sketch, "E31.0.8.0", {"start": v(-6.1, 23.93) * mm, "end": v(-5.6, 23.93) * mm});
            skLineSegment(sketch, "E31.3.8.0", {"start": v(-6.09, 25.93) * mm, "end": v(-6.1, 23.93) * mm, "construction": true});
            skLineSegment(sketch, "E31.6.8.0", {"start": v(-5.6, 24.43) * mm, "end": v(-5.6, 23.93) * mm});
            skLineSegment(sketch, "E31.9.8.0", {"start": v(-6.1, 24.43) * mm, "end": v(-5.6, 24.43) * mm});
            skLineSegment(sketch, "E31.0.9.0", {"start": v(-8.6, 23.93) * mm, "end": v(-8.1, 23.93) * mm});
            skLineSegment(sketch, "E31.3.9.0", {"start": v(-8.59, 25.93) * mm, "end": v(-8.6, 23.93) * mm, "construction": true});
            skLineSegment(sketch, "E31.6.9.0", {"start": v(-8.1, 24.43) * mm, "end": v(-8.1, 23.93) * mm});
            skLineSegment(sketch, "E31.9.9.0", {"start": v(-8.6, 24.43) * mm, "end": v(-8.1, 24.43) * mm});
            skLineSegment(sketch, "E31.0.10.0", {"start": v(-11.1, 23.93) * mm, "end": v(-10.6, 23.93) * mm});
            skLineSegment(sketch, "E31.3.10.0", {"start": v(-11.09, 25.93) * mm, "end": v(-11.1, 23.93) * mm, "construction": true});
            skLineSegment(sketch, "E31.6.10.0", {"start": v(-10.6, 24.43) * mm, "end": v(-10.6, 23.93) * mm});
            skLineSegment(sketch, "E31.9.10.0", {"start": v(-11.1, 24.43) * mm, "end": v(-10.6, 24.43) * mm});
            skLineSegment(sketch, "E31.0.11.0", {"start": v(-13.6, 23.93) * mm, "end": v(-13.1, 23.93) * mm});
            skLineSegment(sketch, "E31.3.11.0", {"start": v(-13.59, 25.93) * mm, "end": v(-13.6, 23.93) * mm, "construction": true});
            skLineSegment(sketch, "E31.6.11.0", {"start": v(-13.1, 24.43) * mm, "end": v(-13.1, 23.93) * mm});
            skLineSegment(sketch, "E31.9.11.0", {"start": v(-13.6, 24.43) * mm, "end": v(-13.1, 24.43) * mm});
            skLineSegment(sketch, "E31.0.12.0", {"start": v(-16.1, 23.93) * mm, "end": v(-15.6, 23.93) * mm});
            skLineSegment(sketch, "E31.3.12.0", {"start": v(-16.09, 25.93) * mm, "end": v(-16.1, 23.93) * mm, "construction": true});
            skLineSegment(sketch, "E31.6.12.0", {"start": v(-15.6, 24.43) * mm, "end": v(-15.6, 23.93) * mm});
            skLineSegment(sketch, "E31.9.12.0", {"start": v(-16.1, 24.43) * mm, "end": v(-15.6, 24.43) * mm});
            skLineSegment(sketch, "E31.0.13.0", {"start": v(-18.6, 23.93) * mm, "end": v(-18.1, 23.93) * mm});
            skLineSegment(sketch, "E31.3.13.0", {"start": v(-18.59, 25.93) * mm, "end": v(-18.6, 23.93) * mm, "construction": true});
            skLineSegment(sketch, "E31.6.13.0", {"start": v(-18.1, 24.43) * mm, "end": v(-18.1, 23.93) * mm});
            skLineSegment(sketch, "E31.9.13.0", {"start": v(-18.6, 24.43) * mm, "end": v(-18.1, 24.43) * mm});
            skLineSegment(sketch, "E31.0.14.0", {"start": v(-21.1, 23.92) * mm, "end": v(-20.6, 23.92) * mm});
            skLineSegment(sketch, "E31.3.14.0", {"start": v(-21.09, 25.92) * mm, "end": v(-21.1, 23.92) * mm, "construction": true});
            skLineSegment(sketch, "E31.6.14.0", {"start": v(-20.6, 24.42) * mm, "end": v(-20.6, 23.92) * mm});
            skLineSegment(sketch, "E31.9.14.0", {"start": v(-21.1, 24.42) * mm, "end": v(-20.6, 24.42) * mm});
            skLineSegment(sketch, "E31.0.15.0", {"start": v(-23.6, 23.92) * mm, "end": v(-23.1, 23.92) * mm});
            skLineSegment(sketch, "E31.3.15.0", {"start": v(-23.59, 25.92) * mm, "end": v(-23.6, 23.92) * mm, "construction": true});
            skLineSegment(sketch, "E31.6.15.0", {"start": v(-23.1, 24.42) * mm, "end": v(-23.1, 23.92) * mm});
            skLineSegment(sketch, "E31.9.15.0", {"start": v(-23.6, 24.42) * mm, "end": v(-23.1, 24.42) * mm});
            skLineSegment(sketch, "E31.0.16.0", {"start": v(-26.1, 23.92) * mm, "end": v(-25.6, 23.92) * mm});
            skLineSegment(sketch, "E31.3.16.0", {"start": v(-26.09, 25.92) * mm, "end": v(-26.1, 23.92) * mm, "construction": true});
            skLineSegment(sketch, "E31.6.16.0", {"start": v(-25.6, 24.42) * mm, "end": v(-25.6, 23.92) * mm});
            skLineSegment(sketch, "E31.9.16.0", {"start": v(-26.1, 24.42) * mm, "end": v(-25.6, 24.42) * mm});
            skLineSegment(sketch, "E31.0.17.0", {"start": v(-28.6, 23.92) * mm, "end": v(-28.1, 23.92) * mm});
            skLineSegment(sketch, "E31.3.17.0", {"start": v(-28.59, 25.92) * mm, "end": v(-28.6, 23.92) * mm, "construction": true});
            skLineSegment(sketch, "E31.6.17.0", {"start": v(-28.1, 24.42) * mm, "end": v(-28.1, 23.92) * mm});
            skLineSegment(sketch, "E31.9.17.0", {"start": v(-28.6, 24.42) * mm, "end": v(-28.1, 24.42) * mm});
            skLineSegment(sketch, "E31.0.18.0", {"start": v(-31.1, 23.92) * mm, "end": v(-30.6, 23.92) * mm});
            skLineSegment(sketch, "E31.3.18.0", {"start": v(-31.09, 25.92) * mm, "end": v(-31.1, 23.92) * mm, "construction": true});
            skLineSegment(sketch, "E31.6.18.0", {"start": v(-30.6, 24.42) * mm, "end": v(-30.6, 23.92) * mm});
            skLineSegment(sketch, "E31.9.18.0", {"start": v(-31.1, 24.42) * mm, "end": v(-30.6, 24.42) * mm});
            skLineSegment(sketch, "E31.0.19.0", {"start": v(-33.6, 23.92) * mm, "end": v(-33.1, 23.92) * mm});
            skLineSegment(sketch, "E31.3.19.0", {"start": v(-33.59, 25.92) * mm, "end": v(-33.6, 23.92) * mm, "construction": true});
            skLineSegment(sketch, "E31.6.19.0", {"start": v(-33.1, 24.42) * mm, "end": v(-33.1, 23.92) * mm});
            skLineSegment(sketch, "E31.9.19.0", {"start": v(-33.6, 24.42) * mm, "end": v(-33.1, 24.42) * mm});
            skLineSegment(sketch, "E32", {"start": v(11.4, 24.43) * mm, "end": v(11.4, 23.93) * mm});
            skLineSegment(sketch, "E33", {"start": v(8.9, 24.43) * mm, "end": v(8.9, 23.93) * mm});
            skLineSegment(sketch, "E34", {"start": v(6.4, 23.93) * mm, "end": v(6.4, 24.43) * mm});
            skLineSegment(sketch, "E35", {"start": v(3.9, 24.43) * mm, "end": v(3.9, 23.93) * mm});
            skLineSegment(sketch, "E36", {"start": v(1.4, 24.43) * mm, "end": v(1.4, 23.93) * mm});
            skLineSegment(sketch, "E37", {"start": v(-1.1, 24.43) * mm, "end": v(-1.1, 23.93) * mm});
            skLineSegment(sketch, "E38", {"start": v(-3.6, 24.43) * mm, "end": v(-3.6, 23.93) * mm});
            skLineSegment(sketch, "E39", {"start": v(-6.1, 24.43) * mm, "end": v(-6.1, 23.93) * mm});
            skLineSegment(sketch, "E40", {"start": v(-8.6, 24.43) * mm, "end": v(-8.6, 23.93) * mm});
            skLineSegment(sketch, "E41", {"start": v(-11.1, 24.43) * mm, "end": v(-11.1, 23.93) * mm});
            skLineSegment(sketch, "E42", {"start": v(-13.6, 24.43) * mm, "end": v(-13.6, 23.93) * mm});
            skLineSegment(sketch, "E43", {"start": v(-16.1, 24.43) * mm, "end": v(-16.1, 23.93) * mm});
            skLineSegment(sketch, "E44", {"start": v(-18.6, 24.43) * mm, "end": v(-18.6, 23.93) * mm});
            skLineSegment(sketch, "E45", {"start": v(-21.1, 24.42) * mm, "end": v(-21.1, 23.92) * mm});
            skLineSegment(sketch, "E46", {"start": v(-23.6, 24.42) * mm, "end": v(-23.6, 23.92) * mm});
            skLineSegment(sketch, "E47", {"start": v(-26.1, 24.42) * mm, "end": v(-26.1, 23.92) * mm});
            skLineSegment(sketch, "E48", {"start": v(-28.6, 24.42) * mm, "end": v(-28.6, 23.92) * mm});
            skLineSegment(sketch, "E49", {"start": v(-31.1, 24.42) * mm, "end": v(-31.1, 23.92) * mm});
            skLineSegment(sketch, "E50", {"start": v(-33.6, 24.42) * mm, "end": v(-33.6, 23.92) * mm});
            skSolve(sketch);
        }
        {
            var Q0;
            Q0=qSketchRegion(id+"F26",true);
            var Q1;
            Q1=qConstructionFilter(qBodyType(qCreatedBy(id+"F26",EDGE),BodyType.WIRE),ConstructionObject.NO);
            extrude(context, id + "F27", {"entities" : qUnion([Q0]), "surfaceEntities" : qUnion([Q1]), "depth" : 6 * mm});
        }
        {
            var Q0;
            Q0=qSketchRegion(id+"F26",true);
            extrude(context, id + "F28", {"entities" : qUnion([Q0]), "operationType" : NewBodyOperationType.ADD, "depth" : -6 * mm});
        }
        {
            var Q0;
            Q0=makeQuery(id+"F1.opExtrude","CAP_FACE",FACE,{"disambiguationData":[OSD([sQuery(id+"F0.wireOp",EDGE,"E0.bottom"),sQuery(id+"F0.wireOp",EDGE,"E0.top"),sQuery(id+"F0.wireOp",EDGE,"E0.left"),sQuery(id+"F0.wireOp",EDGE,"E0.right"),sQuery(id+"F0.wireOp",EDGE,"E2"),sQuery(id+"F0.wireOp",EDGE,"E3"),sQuery(id+"F0.wireOp",EDGE,"E4"),sQuery(id+"F0.wireOp",EDGE,"E5"),sQuery(id+"F0.wireOp",EDGE,"E6.bottom"),sQuery(id+"F0.wireOp",EDGE,"E7.filletArc"),sQuery(id+"F0.wireOp",EDGE,"E8.filletArc"),sQuery(id+"F0.wireOp",EDGE,"E9.filletArc"),sQuery(id+"F0.wireOp",EDGE,"E10.filletArc")])],"isStart":false});
            var sketch = newSketch(context, id + "F29", { "sketchPlane" : qUnion([Q0])});
            skLineSegment(sketch, "E51.bottom", {"start": v(4.16, 13.44) * mm, "end": v(17.16, 13.44) * mm});
            skLineSegment(sketch, "E51.top", {"start": v(4.16, 6.44) * mm, "end": v(17.16, 6.44) * mm});
            skLineSegment(sketch, "E51.left", {"start": v(4.16, 13.44) * mm, "end": v(4.16, 6.44) * mm});
            skLineSegment(sketch, "E51.right", {"start": v(17.16, 13.44) * mm, "end": v(17.16, 6.44) * mm});
            skSolve(sketch);
        }
        {
            var Q0;
            Q0=qSketchRegion(id+"F29",true);
            extrude(context, id + "F30", {"entities" : qUnion([Q0]), "operationType" : NewBodyOperationType.ADD, "depth" : 0.5 * mm});
        }
        {
            var Q0;
            Q0=makeQuery(id+"F1.opExtrude","CAP_FACE",FACE,{"disambiguationData":[OSD([sQuery(id+"F0.wireOp",EDGE,"E0.bottom"),sQuery(id+"F0.wireOp",EDGE,"E0.top"),sQuery(id+"F0.wireOp",EDGE,"E0.left"),sQuery(id+"F0.wireOp",EDGE,"E0.right"),sQuery(id+"F0.wireOp",EDGE,"E2"),sQuery(id+"F0.wireOp",EDGE,"E3"),sQuery(id+"F0.wireOp",EDGE,"E4"),sQuery(id+"F0.wireOp",EDGE,"E5"),sQuery(id+"F0.wireOp",EDGE,"E6.bottom"),sQuery(id+"F0.wireOp",EDGE,"E7.filletArc"),sQuery(id+"F0.wireOp",EDGE,"E8.filletArc"),sQuery(id+"F0.wireOp",EDGE,"E9.filletArc"),sQuery(id+"F0.wireOp",EDGE,"E10.filletArc")])],"isStart":false});
            var sketch = newSketch(context, id + "F31", { "sketchPlane" : qUnion([Q0])});
            skLineSegment(sketch, "E52.bottom", {"start": v(19.16, 21.44) * mm, "end": v(23.16, 21.44) * mm});
            skLineSegment(sketch, "E52.top", {"start": v(19.16, 17.44) * mm, "end": v(23.16, 17.44) * mm});
            skLineSegment(sketch, "E52.left", {"start": v(19.16, 21.44) * mm, "end": v(19.16, 17.44) * mm});
            skLineSegment(sketch, "E52.right", {"start": v(23.16, 21.44) * mm, "end": v(23.16, 17.44) * mm});
            skLineSegment(sketch, "E53.bottom", {"start": v(-22.84, 18.44) * mm, "end": v(-18.84, 18.44) * mm});
            skLineSegment(sketch, "E53.top", {"start": v(-22.84, 14.44) * mm, "end": v(-18.84, 14.44) * mm});
            skLineSegment(sketch, "E53.left", {"start": v(-22.84, 18.44) * mm, "end": v(-22.84, 14.44) * mm});
            skLineSegment(sketch, "E53.right", {"start": v(-18.84, 18.44) * mm, "end": v(-18.84, 14.44) * mm});
            skLineSegment(sketch, "E54.bottom", {"start": v(-13.84, -2.56) * mm, "end": v(-9.84, -2.56) * mm});
            skLineSegment(sketch, "E54.top", {"start": v(-13.84, -6.56) * mm, "end": v(-9.84, -6.56) * mm});
            skLineSegment(sketch, "E54.left", {"start": v(-13.84, -2.56) * mm, "end": v(-13.84, -6.56) * mm});
            skLineSegment(sketch, "E54.right", {"start": v(-9.84, -2.56) * mm, "end": v(-9.84, -6.56) * mm});
            skSolve(sketch);
        }
        {
            var Q0;
            Q0=qSketchRegion(id+"F31",true);
            extrude(context, id + "F32", {"entities" : qUnion([Q0]), "operationType" : NewBodyOperationType.ADD, "depth" : 1.5 * mm});
        }
        {
            var Q0;
            Q0=makeQuery(id+"F1.opExtrude","CAP_FACE",FACE,{"disambiguationData":[OSD([sQuery(id+"F0.wireOp",EDGE,"E0.bottom"),sQuery(id+"F0.wireOp",EDGE,"E0.top"),sQuery(id+"F0.wireOp",EDGE,"E0.left"),sQuery(id+"F0.wireOp",EDGE,"E0.right"),sQuery(id+"F0.wireOp",EDGE,"E2"),sQuery(id+"F0.wireOp",EDGE,"E3"),sQuery(id+"F0.wireOp",EDGE,"E4"),sQuery(id+"F0.wireOp",EDGE,"E5"),sQuery(id+"F0.wireOp",EDGE,"E6.bottom"),sQuery(id+"F0.wireOp",EDGE,"E7.filletArc"),sQuery(id+"F0.wireOp",EDGE,"E8.filletArc"),sQuery(id+"F0.wireOp",EDGE,"E9.filletArc"),sQuery(id+"F0.wireOp",EDGE,"E10.filletArc")])],"isStart":false});
            var sketch = newSketch(context, id + "F33", { "sketchPlane" : qUnion([Q0])});
            skLineSegment(sketch, "E55.bottom", {"start": v(0.16, 20.44) * mm, "end": v(1.16, 20.44) * mm});
            skLineSegment(sketch, "E55.top", {"start": v(0.16, 19.44) * mm, "end": v(1.16, 19.44) * mm});
            skLineSegment(sketch, "E55.left", {"start": v(0.16, 20.44) * mm, "end": v(0.16, 19.44) * mm});
            skLineSegment(sketch, "E55.right", {"start": v(1.16, 20.44) * mm, "end": v(1.16, 19.44) * mm});
            skLineSegment(sketch, "E56.bottom", {"start": v(5.16, 20.44) * mm, "end": v(6.16, 20.44) * mm});
            skLineSegment(sketch, "E56.top", {"start": v(5.16, 19.44) * mm, "end": v(6.16, 19.44) * mm});
            skLineSegment(sketch, "E56.left", {"start": v(5.16, 20.44) * mm, "end": v(5.16, 19.44) * mm});
            skLineSegment(sketch, "E56.right", {"start": v(6.16, 20.44) * mm, "end": v(6.16, 19.44) * mm});
            skSolve(sketch);
        }
        {
            var Q0;
            Q0=qSketchRegion(id+"F33",true);
            extrude(context, id + "F34", {"entities" : qUnion([Q0]), "operationType" : NewBodyOperationType.ADD, "depth" : .5 * mm});
        }
        {
            var Q0;
            Q0=makeQuery(id+"F1.opExtrude","CAP_FACE",FACE,{"disambiguationData":[OSD([sQuery(id+"F0.wireOp",EDGE,"E0.bottom"),sQuery(id+"F0.wireOp",EDGE,"E0.top"),sQuery(id+"F0.wireOp",EDGE,"E0.left"),sQuery(id+"F0.wireOp",EDGE,"E0.right"),sQuery(id+"F0.wireOp",EDGE,"E2"),sQuery(id+"F0.wireOp",EDGE,"E3"),sQuery(id+"F0.wireOp",EDGE,"E4"),sQuery(id+"F0.wireOp",EDGE,"E5"),sQuery(id+"F0.wireOp",EDGE,"E6.bottom"),sQuery(id+"F0.wireOp",EDGE,"E7.filletArc"),sQuery(id+"F0.wireOp",EDGE,"E8.filletArc"),sQuery(id+"F0.wireOp",EDGE,"E9.filletArc"),sQuery(id+"F0.wireOp",EDGE,"E10.filletArc")])],"isStart":false});
            var sketch = newSketch(context, id + "F35", { "sketchPlane" : qUnion([Q0])});
            skLineSegment(sketch, "E57.bottom", {"start": v(-12.74, 19.44) * mm, "end": v(-2.84, 9.54) * mm});
            skLineSegment(sketch, "E57.top", {"start": v(-22.64, 9.54) * mm, "end": v(-12.74, -0.36) * mm});
            skLineSegment(sketch, "E57.left", {"start": v(-12.74, 19.44) * mm, "end": v(-22.64, 9.54) * mm});
            skLineSegment(sketch, "E57.right", {"start": v(-2.84, 9.54) * mm, "end": v(-12.74, -0.36) * mm});
            skSolve(sketch);
        }
        {
            var Q0;
            Q0=qSketchRegion(id+"F35",true);
            extrude(context, id + "F36", {"entities" : qUnion([Q0]), "operationType" : NewBodyOperationType.ADD, "depth" : .5 * mm});
        }
        {
            var Q0;
            Q0=qSketchRegion(id+"F18",true);
            extrude(context, id + "F37", {"entities" : qUnion([Q0]), "operationType" : NewBodyOperationType.ADD, "depth" : -6 * mm});
        }
        {
            var Q0;
            Q0=makeQuery(id+"F0.imprint","IMPRINT",FACE,{"disambiguationData":[TD([[makeQuery(id+"F0.imprint","IMPRINT",EDGE,{"derivedFrom":sQuery(id+"F0.wireOp",EDGE,"E0.bottom")}),-1.0]])]});
            var sketch = newSketch(context, id + "F38", { "sketchPlane" : qUnion([Q0])});
            skLineSegment(sketch, "E58.bottom", {"start": v(-8.34, -19.56) * mm, "end": v(8.16, -19.56) * mm});
            skLineSegment(sketch, "E58.top", {"start": v(-8.34, -13.56) * mm, "end": v(8.16, -13.56) * mm});
            skLineSegment(sketch, "E58.left", {"start": v(-8.34, -19.56) * mm, "end": v(-8.34, -13.56) * mm});
            skLineSegment(sketch, "E58.right", {"start": v(8.16, -19.56) * mm, "end": v(8.16, -13.56) * mm});
            skSolve(sketch);
        }
        {
            var Q0;
            Q0=qSketchRegion(id+"F38",true);
            extrude(context, id + "F39", {"entities" : qUnion([Q0]), "operationType" : NewBodyOperationType.ADD, "depth" : -2 * mm});
        }
        {
            var Q0;
            Q0=makeQuery(id+"F0.imprint","IMPRINT",FACE,{"disambiguationData":[TD([[makeQuery(id+"F0.imprint","IMPRINT",EDGE,{"derivedFrom":sQuery(id+"F0.wireOp",EDGE,"E0.bottom")}),-1.0]])]});
            var sketch = newSketch(context, id + "F40", { "sketchPlane" : qUnion([Q0])});
            skLineSegment(sketch, "E59.bottom", {"start": v(-3.34, -8.56) * mm, "end": v(1.16, -8.56) * mm});
            skLineSegment(sketch, "E59.top", {"start": v(-3.34, -4.06) * mm, "end": v(1.16, -4.06) * mm});
            skLineSegment(sketch, "E59.left", {"start": v(-3.34, -8.56) * mm, "end": v(-3.34, -4.06) * mm});
            skLineSegment(sketch, "E59.right", {"start": v(1.16, -8.56) * mm, "end": v(1.16, -4.06) * mm});
            skSolve(sketch);
        }
        {
            var Q0;
            Q0=qSketchRegion(id+"F40",true);
            extrude(context, id + "F41", {"entities" : qUnion([Q0]), "operationType" : NewBodyOperationType.ADD, "depth" : -2 * mm});
        }
        {
            var Q0;
            Q0=makeQuery(id+"F0.imprint","IMPRINT",FACE,{"disambiguationData":[TD([[makeQuery(id+"F0.imprint","IMPRINT",EDGE,{"derivedFrom":sQuery(id+"F0.wireOp",EDGE,"E0.bottom")}),-1.0]])]});
            var sketch = newSketch(context, id + "F42", { "sketchPlane" : qUnion([Q0])});
            skLineSegment(sketch, "E60.bottom", {"start": v(3.66, 4.94) * mm, "end": v(17.16, 4.94) * mm});
            skLineSegment(sketch, "E60.top", {"start": v(3.66, 12.44) * mm, "end": v(17.16, 12.44) * mm});
            skLineSegment(sketch, "E60.left", {"start": v(3.66, 4.94) * mm, "end": v(3.66, 12.44) * mm});
            skLineSegment(sketch, "E60.right", {"start": v(17.16, 4.94) * mm, "end": v(17.16, 12.44) * mm});
            skSolve(sketch);
        }
        {
            var Q0;
            Q0=qSketchRegion(id+"F42",true);
            extrude(context, id + "F43", {"entities" : qUnion([Q0]), "operationType" : NewBodyOperationType.ADD, "depth" : -0.5 * mm});
        }
        {
            var Q0;
            Q0=makeQuery(id+"F0.imprint","IMPRINT",FACE,{"disambiguationData":[TD([[makeQuery(id+"F0.imprint","IMPRINT",EDGE,{"derivedFrom":sQuery(id+"F0.wireOp",EDGE,"E0.bottom")}),-1.0]])]});
            var sketch = newSketch(context, id + "F44", { "sketchPlane" : qUnion([Q0])});
            skLineSegment(sketch, "E61.bottom", {"start": v(14.66, -5.56) * mm, "end": v(23.66, -5.56) * mm});
            skLineSegment(sketch, "E61.top", {"start": v(14.66, 0.44) * mm, "end": v(23.66, 0.44) * mm});
            skLineSegment(sketch, "E61.left", {"start": v(14.66, -5.56) * mm, "end": v(14.66, 0.44) * mm});
            skLineSegment(sketch, "E61.right", {"start": v(23.66, -5.56) * mm, "end": v(23.66, 0.44) * mm});
            skSolve(sketch);
        }
        {
            var Q0;
            Q0=qSketchRegion(id+"F44",true);
            extrude(context, id + "F45", {"entities" : qUnion([Q0]), "operationType" : NewBodyOperationType.ADD, "depth" : -2 * mm});
        }
        {
            var Q0;
            Q0=makeQuery(id+"F0.imprint","IMPRINT",FACE,{"disambiguationData":[TD([[makeQuery(id+"F0.imprint","IMPRINT",EDGE,{"derivedFrom":sQuery(id+"F0.wireOp",EDGE,"E0.bottom")}),-1.0]])]});
            var sketch = newSketch(context, id + "F46", { "sketchPlane" : qUnion([Q0])});
            skLineSegment(sketch, "E62.bottom", {"start": v(-36.84, 11.44) * mm, "end": v(-35.84, 11.44) * mm});
            skLineSegment(sketch, "E62.top", {"start": v(-36.84, 12.44) * mm, "end": v(-35.84, 12.44) * mm});
            skLineSegment(sketch, "E62.left", {"start": v(-36.84, 11.44) * mm, "end": v(-36.84, 12.44) * mm});
            skLineSegment(sketch, "E62.right", {"start": v(-35.84, 11.44) * mm, "end": v(-35.84, 12.44) * mm});
            skLineSegment(sketch, "E63.bottom", {"start": v(-29.84, 11.44) * mm, "end": v(-28.84, 11.44) * mm});
            skLineSegment(sketch, "E63.top", {"start": v(-29.84, 12.44) * mm, "end": v(-28.84, 12.44) * mm});
            skLineSegment(sketch, "E63.left", {"start": v(-29.84, 11.44) * mm, "end": v(-29.84, 12.44) * mm});
            skLineSegment(sketch, "E63.right", {"start": v(-28.84, 11.44) * mm, "end": v(-28.84, 12.44) * mm});
            skLineSegment(sketch, "E64.bottom", {"start": v(-36.84, 17.94) * mm, "end": v(-35.84, 17.94) * mm});
            skLineSegment(sketch, "E64.top", {"start": v(-36.84, 18.94) * mm, "end": v(-35.84, 18.94) * mm});
            skLineSegment(sketch, "E64.left", {"start": v(-36.84, 17.94) * mm, "end": v(-36.84, 18.94) * mm});
            skLineSegment(sketch, "E64.right", {"start": v(-35.84, 17.94) * mm, "end": v(-35.84, 18.94) * mm});
            skLineSegment(sketch, "E65.bottom", {"start": v(-29.84, 17.94) * mm, "end": v(-28.84, 17.94) * mm});
            skLineSegment(sketch, "E65.top", {"start": v(-29.84, 18.94) * mm, "end": v(-28.84, 18.94) * mm});
            skLineSegment(sketch, "E65.left", {"start": v(-29.84, 17.94) * mm, "end": v(-29.84, 18.94) * mm});
            skLineSegment(sketch, "E65.right", {"start": v(-28.84, 17.94) * mm, "end": v(-28.84, 18.94) * mm});
            skLineSegment(sketch, "E66.bottom", {"start": v(-34.84, 9.44) * mm, "end": v(-33.84, 9.44) * mm});
            skLineSegment(sketch, "E66.top", {"start": v(-34.84, 10.44) * mm, "end": v(-33.84, 10.44) * mm});
            skLineSegment(sketch, "E66.left", {"start": v(-34.84, 9.44) * mm, "end": v(-34.84, 10.44) * mm});
            skLineSegment(sketch, "E66.right", {"start": v(-33.84, 9.44) * mm, "end": v(-33.84, 10.44) * mm});
            skLineSegment(sketch, "E67.bottom", {"start": v(-34.84, -1.06) * mm, "end": v(-33.84, -1.06) * mm});
            skLineSegment(sketch, "E67.top", {"start": v(-34.84, -0.06) * mm, "end": v(-33.84, -0.06) * mm});
            skLineSegment(sketch, "E67.left", {"start": v(-34.84, -1.06) * mm, "end": v(-34.84, -0.06) * mm});
            skLineSegment(sketch, "E67.right", {"start": v(-33.84, -1.06) * mm, "end": v(-33.84, -0.06) * mm});
            skLineSegment(sketch, "E68.bottom", {"start": v(-41.34, -5.06) * mm, "end": v(-40.84, -5.06) * mm});
            skLineSegment(sketch, "E68.top", {"start": v(-41.34, -4.56) * mm, "end": v(-40.84, -4.56) * mm});
            skLineSegment(sketch, "E68.left", {"start": v(-41.34, -5.06) * mm, "end": v(-41.34, -4.56) * mm});
            skLineSegment(sketch, "E68.right", {"start": v(-40.84, -5.06) * mm, "end": v(-40.84, -4.56) * mm});
            skLineSegment(sketch, "E69.bottom", {"start": v(-41.34, -2.56) * mm, "end": v(-40.84, -2.56) * mm});
            skLineSegment(sketch, "E69.top", {"start": v(-41.34, -2.06) * mm, "end": v(-40.84, -2.06) * mm});
            skLineSegment(sketch, "E69.left", {"start": v(-41.34, -2.56) * mm, "end": v(-41.34, -2.06) * mm});
            skLineSegment(sketch, "E69.right", {"start": v(-40.84, -2.56) * mm, "end": v(-40.84, -2.06) * mm});
            skLineSegment(sketch, "E70.bottom", {"start": v(-30.84, -1.66) * mm, "end": v(-30.34, -1.66) * mm});
            skLineSegment(sketch, "E70.top", {"start": v(-30.84, -1.16) * mm, "end": v(-30.34, -1.16) * mm});
            skLineSegment(sketch, "E70.left", {"start": v(-30.84, -1.66) * mm, "end": v(-30.84, -1.16) * mm});
            skLineSegment(sketch, "E70.right", {"start": v(-30.34, -1.66) * mm, "end": v(-30.34, -1.16) * mm});
            skLineSegment(sketch, "E71.bottom", {"start": v(-28.64, -2.86) * mm, "end": v(-28.14, -2.86) * mm});
            skLineSegment(sketch, "E71.top", {"start": v(-28.64, -2.36) * mm, "end": v(-28.14, -2.36) * mm});
            skLineSegment(sketch, "E71.left", {"start": v(-28.64, -2.86) * mm, "end": v(-28.64, -2.36) * mm});
            skLineSegment(sketch, "E71.right", {"start": v(-28.14, -2.86) * mm, "end": v(-28.14, -2.36) * mm});
            skLineSegment(sketch, "E72.bottom", {"start": v(-30.84, 1.04) * mm, "end": v(-30.34, 1.04) * mm});
            skLineSegment(sketch, "E72.top", {"start": v(-30.84, 1.54) * mm, "end": v(-30.34, 1.54) * mm});
            skLineSegment(sketch, "E72.left", {"start": v(-30.84, 1.04) * mm, "end": v(-30.84, 1.54) * mm});
            skLineSegment(sketch, "E72.right", {"start": v(-30.34, 1.04) * mm, "end": v(-30.34, 1.54) * mm});
            skLineSegment(sketch, "E73.bottom", {"start": v(-28.64, -0.16) * mm, "end": v(-28.14, -0.16) * mm});
            skLineSegment(sketch, "E73.top", {"start": v(-28.64, 0.34) * mm, "end": v(-28.14, 0.34) * mm});
            skLineSegment(sketch, "E73.left", {"start": v(-28.64, -0.16) * mm, "end": v(-28.64, 0.34) * mm});
            skLineSegment(sketch, "E73.right", {"start": v(-28.14, -0.16) * mm, "end": v(-28.14, 0.34) * mm});
            skLineSegment(sketch, "E74.bottom", {"start": v(-30.84, 3.74) * mm, "end": v(-30.34, 3.74) * mm});
            skLineSegment(sketch, "E74.top", {"start": v(-30.84, 4.24) * mm, "end": v(-30.34, 4.24) * mm});
            skLineSegment(sketch, "E74.left", {"start": v(-30.84, 3.74) * mm, "end": v(-30.84, 4.24) * mm});
            skLineSegment(sketch, "E74.right", {"start": v(-30.34, 3.74) * mm, "end": v(-30.34, 4.24) * mm});
            skLineSegment(sketch, "E75.bottom", {"start": v(-28.64, 2.54) * mm, "end": v(-28.14, 2.54) * mm});
            skLineSegment(sketch, "E75.top", {"start": v(-28.64, 3.04) * mm, "end": v(-28.14, 3.04) * mm});
            skLineSegment(sketch, "E75.left", {"start": v(-28.64, 2.54) * mm, "end": v(-28.64, 3.04) * mm});
            skLineSegment(sketch, "E75.right", {"start": v(-28.14, 2.54) * mm, "end": v(-28.14, 3.04) * mm});
            skLineSegment(sketch, "E76.bottom", {"start": v(-30.84, 6.44) * mm, "end": v(-30.34, 6.44) * mm});
            skLineSegment(sketch, "E76.top", {"start": v(-30.84, 6.94) * mm, "end": v(-30.34, 6.94) * mm});
            skLineSegment(sketch, "E76.left", {"start": v(-30.84, 6.44) * mm, "end": v(-30.84, 6.94) * mm});
            skLineSegment(sketch, "E76.right", {"start": v(-30.34, 6.44) * mm, "end": v(-30.34, 6.94) * mm});
            skLineSegment(sketch, "E77.bottom", {"start": v(-28.64, 5.24) * mm, "end": v(-28.14, 5.24) * mm});
            skLineSegment(sketch, "E77.top", {"start": v(-28.64, 5.74) * mm, "end": v(-28.14, 5.74) * mm});
            skLineSegment(sketch, "E77.left", {"start": v(-28.64, 5.24) * mm, "end": v(-28.64, 5.74) * mm});
            skLineSegment(sketch, "E77.right", {"start": v(-28.14, 5.24) * mm, "end": v(-28.14, 5.74) * mm});
            skLineSegment(sketch, "E78.bottom", {"start": v(-41.34, 8.94) * mm, "end": v(-40.84, 8.94) * mm});
            skLineSegment(sketch, "E78.top", {"start": v(-41.34, 9.44) * mm, "end": v(-40.84, 9.44) * mm});
            skLineSegment(sketch, "E78.left", {"start": v(-41.34, 8.94) * mm, "end": v(-41.34, 9.44) * mm});
            skLineSegment(sketch, "E78.right", {"start": v(-40.84, 8.94) * mm, "end": v(-40.84, 9.44) * mm});
            skLineSegment(sketch, "E79.bottom", {"start": v(-41.34, 6.44) * mm, "end": v(-40.84, 6.44) * mm});
            skLineSegment(sketch, "E79.top", {"start": v(-41.34, 6.94) * mm, "end": v(-40.84, 6.94) * mm});
            skLineSegment(sketch, "E79.left", {"start": v(-41.34, 6.44) * mm, "end": v(-41.34, 6.94) * mm});
            skLineSegment(sketch, "E79.right", {"start": v(-40.84, 6.44) * mm, "end": v(-40.84, 6.94) * mm});
            skSolve(sketch);
        }
        {
            var Q0;
            Q0=qSketchRegion(id+"F46",true);
            extrude(context, id + "F47", {"entities" : qUnion([Q0]), "operationType" : NewBodyOperationType.ADD, "depth" : -3 * mm});
        }
        {
            var Q0;
            Q0=makeQuery(id+"F0.imprint","IMPRINT",FACE,{"disambiguationData":[TD([[makeQuery(id+"F0.imprint","IMPRINT",EDGE,{"derivedFrom":sQuery(id+"F0.wireOp",EDGE,"E0.bottom")}),-1.0]])]});
            var sketch = newSketch(context, id + "F48", { "sketchPlane" : qUnion([Q0])});
            skLineSegment(sketch, "E80.bottom", {"start": v(-38.84, -5.06) * mm, "end": v(-35.84, -5.06) * mm});
            skLineSegment(sketch, "E80.top", {"start": v(-38.84, -2.06) * mm, "end": v(-35.84, -2.06) * mm});
            skLineSegment(sketch, "E80.left", {"start": v(-38.84, -5.06) * mm, "end": v(-38.84, -2.06) * mm});
            skLineSegment(sketch, "E80.right", {"start": v(-35.84, -5.06) * mm, "end": v(-35.84, -2.06) * mm});
            skLineSegment(sketch, "E81.bottom", {"start": v(-38.84, 6.44) * mm, "end": v(-35.84, 6.44) * mm});
            skLineSegment(sketch, "E81.top", {"start": v(-38.84, 9.44) * mm, "end": v(-35.84, 9.44) * mm});
            skLineSegment(sketch, "E81.left", {"start": v(-38.84, 6.44) * mm, "end": v(-38.84, 9.44) * mm});
            skLineSegment(sketch, "E81.right", {"start": v(-35.84, 6.44) * mm, "end": v(-35.84, 9.44) * mm});
            skLineSegment(sketch, "E82.bottom", {"start": v(-25.84, -12.56) * mm, "end": v(-25.34, -12.56) * mm});
            skLineSegment(sketch, "E82.top", {"start": v(-25.84, -10.56) * mm, "end": v(-25.34, -10.56) * mm});
            skLineSegment(sketch, "E82.left", {"start": v(-25.84, -12.56) * mm, "end": v(-25.84, -10.56) * mm});
            skLineSegment(sketch, "E82.right", {"start": v(-25.34, -12.56) * mm, "end": v(-25.34, -10.56) * mm});
            skLineSegment(sketch, "E83.bottom", {"start": v(-11.34, -12.56) * mm, "end": v(-10.84, -12.56) * mm});
            skLineSegment(sketch, "E83.top", {"start": v(-11.34, -10.56) * mm, "end": v(-10.84, -10.56) * mm});
            skLineSegment(sketch, "E83.left", {"start": v(-11.34, -12.56) * mm, "end": v(-11.34, -10.56) * mm});
            skLineSegment(sketch, "E83.right", {"start": v(-10.84, -12.56) * mm, "end": v(-10.84, -10.56) * mm});
            skLineSegment(sketch, "E84.bottom", {"start": v(-25.84, -17.56) * mm, "end": v(-25.34, -17.56) * mm});
            skLineSegment(sketch, "E84.top", {"start": v(-25.84, -17.06) * mm, "end": v(-25.34, -17.06) * mm});
            skLineSegment(sketch, "E84.left", {"start": v(-25.84, -17.56) * mm, "end": v(-25.84, -17.06) * mm});
            skLineSegment(sketch, "E84.right", {"start": v(-25.34, -17.56) * mm, "end": v(-25.34, -17.06) * mm});
            skLineSegment(sketch, "E85.bottom", {"start": v(-11.34, -17.56) * mm, "end": v(-10.84, -17.56) * mm});
            skLineSegment(sketch, "E85.top", {"start": v(-11.34, -17.06) * mm, "end": v(-10.84, -17.06) * mm});
            skLineSegment(sketch, "E85.left", {"start": v(-11.34, -17.56) * mm, "end": v(-11.34, -17.06) * mm});
            skLineSegment(sketch, "E85.right", {"start": v(-10.84, -17.56) * mm, "end": v(-10.84, -17.06) * mm});
            skLineSegment(sketch, "E86.bottom", {"start": v(11.16, -13.56) * mm, "end": v(12.16, -13.56) * mm});
            skLineSegment(sketch, "E86.top", {"start": v(11.16, -12.56) * mm, "end": v(12.16, -12.56) * mm});
            skLineSegment(sketch, "E86.left", {"start": v(11.16, -13.56) * mm, "end": v(11.16, -12.56) * mm});
            skLineSegment(sketch, "E86.right", {"start": v(12.16, -13.56) * mm, "end": v(12.16, -12.56) * mm});
            skLineSegment(sketch, "E87.bottom", {"start": v(12.66, -10.56) * mm, "end": v(13.66, -10.56) * mm});
            skLineSegment(sketch, "E87.top", {"start": v(12.66, -9.56) * mm, "end": v(13.66, -9.56) * mm});
            skLineSegment(sketch, "E87.left", {"start": v(12.66, -10.56) * mm, "end": v(12.66, -9.56) * mm});
            skLineSegment(sketch, "E87.right", {"start": v(13.66, -10.56) * mm, "end": v(13.66, -9.56) * mm});
            skLineSegment(sketch, "E88.bottom", {"start": v(16.16, -11.56) * mm, "end": v(17.16, -11.56) * mm});
            skLineSegment(sketch, "E88.top", {"start": v(16.16, -10.56) * mm, "end": v(17.16, -10.56) * mm});
            skLineSegment(sketch, "E88.left", {"start": v(16.16, -11.56) * mm, "end": v(16.16, -10.56) * mm});
            skLineSegment(sketch, "E88.right", {"start": v(17.16, -11.56) * mm, "end": v(17.16, -10.56) * mm});
            skSolve(sketch);
        }
        {
            var Q0;
            Q0=qSketchRegion(id+"F48",true);
            extrude(context, id + "F49", {"entities" : qUnion([Q0]), "operationType" : NewBodyOperationType.ADD, "depth" : -2 * mm});
        }
    });
